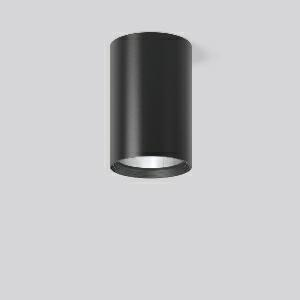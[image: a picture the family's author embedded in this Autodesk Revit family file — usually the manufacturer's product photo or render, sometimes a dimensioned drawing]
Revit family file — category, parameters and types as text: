
# Revit family: heledon_maxi_a_931245_003_2_76_9faa
name_source: partatom
category: Lighting Fixtures
units: mm (PartAtom-declared; Revit-internal decimal feet)

## family parameters
Cut with Voids When Loaded = No
Host = Face
Light Source = No
Part Type = Normal
Room Calculation Point = No
Round Connector Dimension = Use Diameter
Shared = No

## types (1)
- HELEDON maxi A (1 x LED Modul 927 bakery, 3400 lm, 2700)
    Apparent Load = 33 VA
    Approval mark = CE
    CIE Flux Codes = 100 100 100 100 100
    Color Rendering = 90
    Color Temperature = 2700
    Default Elevation = 1800 mm
    Description = Series: HELEDON maxi
Cylindrical surface-mounted downlight. Housing: die-cast aluminium, powder-coated. Internal ceiling frame polycarbonate with bayonet mounting. Black plastic ring and recessed LED to prevent glare from the side. Optical assembly with reflector made of MIRO-Silver with 98% total light reflection for outstanding efficiency - can be changed without tools. Special LED for illumination of pastries included. Suitable for Ceiling mounting. Easy installation with a separate ceiling frame with bayonet mounting and plug connection. Driver integrated. Connected via plug-in connector. High quality converter without flickering and stroboscopic effect. The following accessories can be mounted without use of tools: interchangeable lenses, decorative glasses, honeycomb louvre, clear and frosted diffusers, white interchangeable plastic ring. 
Colour: deep black, matt (RAL 9005)
Diameter: 123 mm
Height: 183 mm
Lamp: LED
Socket: without socket
Colour temperature: bakery
Colour rendering index (CRI): 97
System power: 33 W
Rated luminous flux: 3400 lm
Luminous efficiency: 103 lm/W
Control gear: Converter, dimmable, DALI
Protection class: I
Type of protection: IP 20
    Height = 183 mm
    Lamp = 1 x LED Modul 927 bakery
    Lamp Light Flux = 3400 lm
    Lamp count = 1
    Length = 123 mm
    Lifetime = 50000 h
    Luminous efficacy = 103 lm/W
    Manufacturer = RZB
    ModVariant = No
    Model = 931245.003.2.76
    Mounting Place = Ceiling
    Mounting Type = Surface mounted
    Number of Poles = 1
    OnlyDefault = Yes
    Power Factor = 1
    Product Name = HELEDON maxi A
    Product group = Surface mounted downlights
    ProductGroupID = 302
    Protection Class = Protection class I
    Protection Degree = IP 20
    RLX_Detail_Level = 1
    RLX_Emergency_Light_Flux = 0 lm
    RLX_Emergency_Type = 0
    RLX_Emergency_Type_DB = No
    RlxData = <blob elided: 98289 chars, md5=121fea73>
    Socket = socket
    Standby Power = 0 W
    System Light Flux = 3400 lm
    System Power = 33 W
    Type Comments = Product without accessories
    Type Image = 931192.003.jpg
    URL = http://relux.com
    VarID = ---
    Voltage = 230 V
    Voltage Range = 220-240 V
    Weight = 0.00 kg
    Width = 0 mm  [stored 0 ft]

note: [stored X ft] marks values corroborated as IEEE doubles in the binary element streams (Revit-internal decimal feet)

## geometry (parser evidence)
native form markers: Blend x4, Sweep x9
no freeform markers — native parametric forms only
